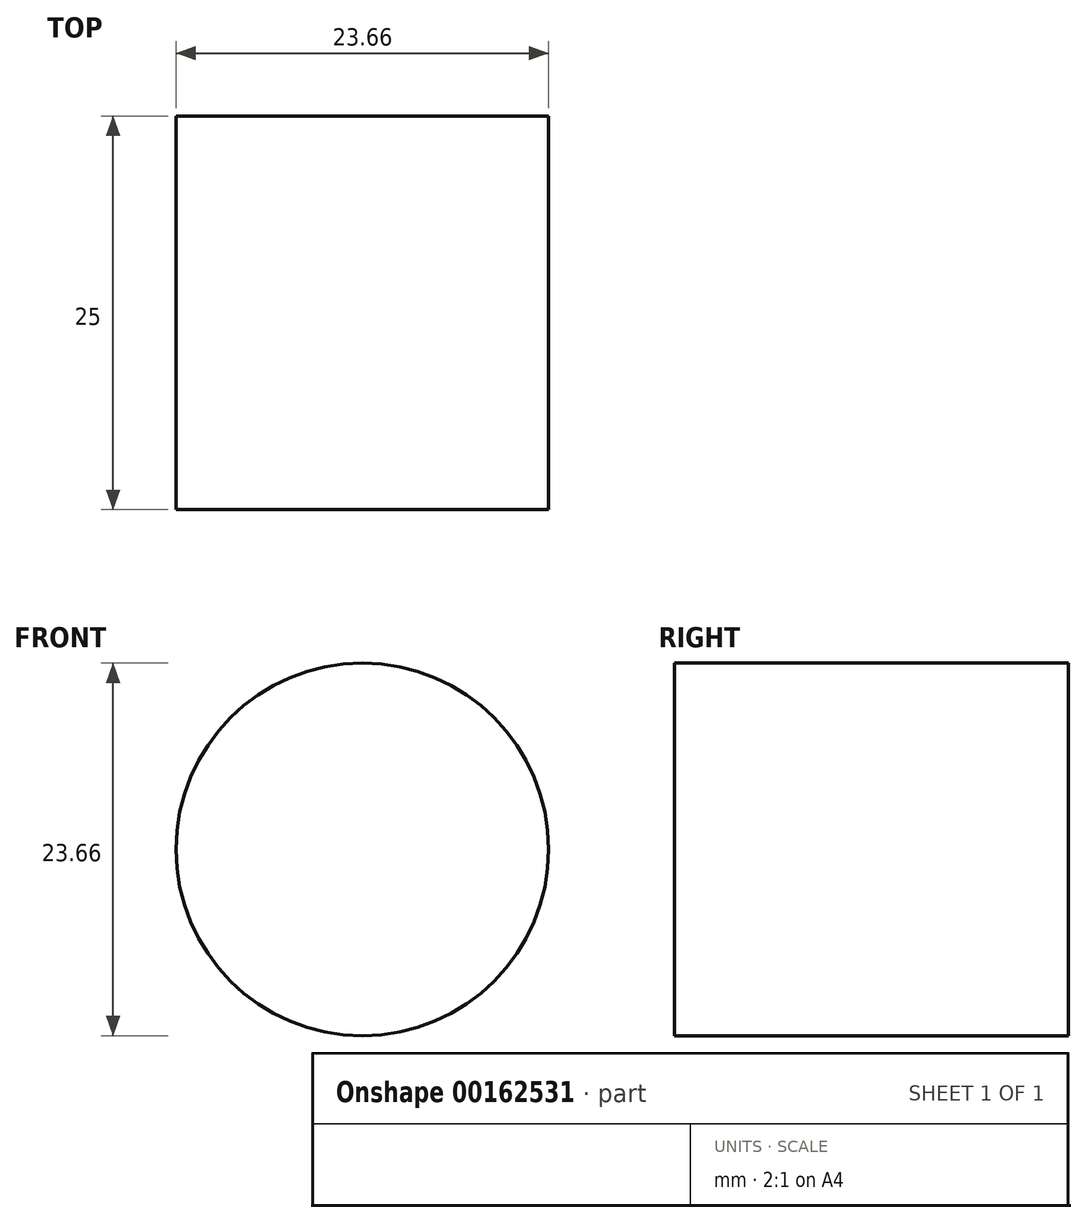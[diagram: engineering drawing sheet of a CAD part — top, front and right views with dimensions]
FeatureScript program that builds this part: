
annotation { "Feature Type Name" : "Feature", "Feature Type Description" : "" }
export const myFeature = defineFeature(function(context is Context, id is Id, definition is map)
    precondition{}
    {
        {
            var Q0;
            Q0=qCreatedBy(makeId("Front.planeOp"),FACE);
            var sketch = newSketch(context, id + "F0", { "sketchPlane" : qUnion([Q0])});
            skLineSegment(sketch, "E0", {"start": v(0, 0) * mm, "end": v(0, 95.84) * mm});
            skCircle(sketch, "E1", {"center": v(0, 0) * mm, "radius": 11.83 * mm});
            skSolve(sketch);
        }
        {
            var Q0;
            Q0=qSketchRegion(id+"F0",true);
            extrude(context, id + "F1", {"entities" : qUnion([Q0]), "depth" : 25 * mm});
        }
    });
